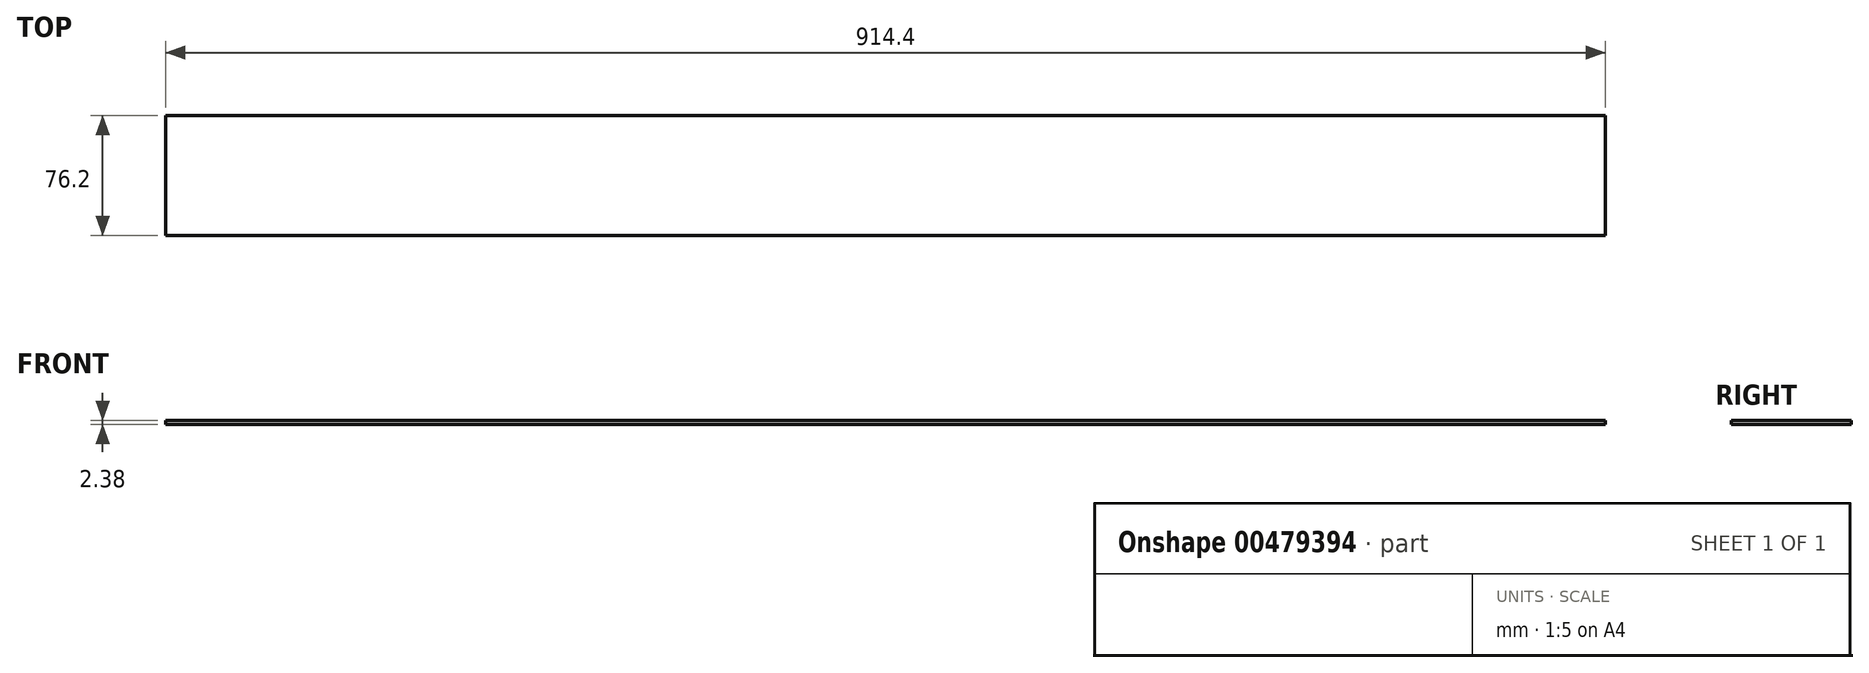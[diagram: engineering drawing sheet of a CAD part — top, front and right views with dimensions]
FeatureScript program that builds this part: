
annotation { "Feature Type Name" : "Feature", "Feature Type Description" : "" }
export const myFeature = defineFeature(function(context is Context, id is Id, definition is map)
    precondition{}
    {
        {
            var Q0;
            Q0=qCreatedBy(makeId("Top.planeOp"),FACE);
            var sketch = newSketch(context, id + "F0", { "sketchPlane" : qUnion([Q0])});
            skLineSegment(sketch, "E0.bottom", {"start": v(0, 0) * mm, "end": v(914.4, 0) * mm});
            skLineSegment(sketch, "E0.top", {"start": v(0, -76.2) * mm, "end": v(914.4, -76.2) * mm});
            skLineSegment(sketch, "E0.left", {"start": v(0, 0) * mm, "end": v(0, -76.2) * mm});
            skLineSegment(sketch, "E0.right", {"start": v(914.4, 0) * mm, "end": v(914.4, -76.2) * mm});
            skSolve(sketch);
        }
        {
            var Q0;
            Q0 = qSketchRegion(id + "F0", true);
            extrude(context, id + "F1", {"entities" : qUnion([Q0]), "oppositeDirection" : true, "depth" : 2.38 * mm});
        }
    });
